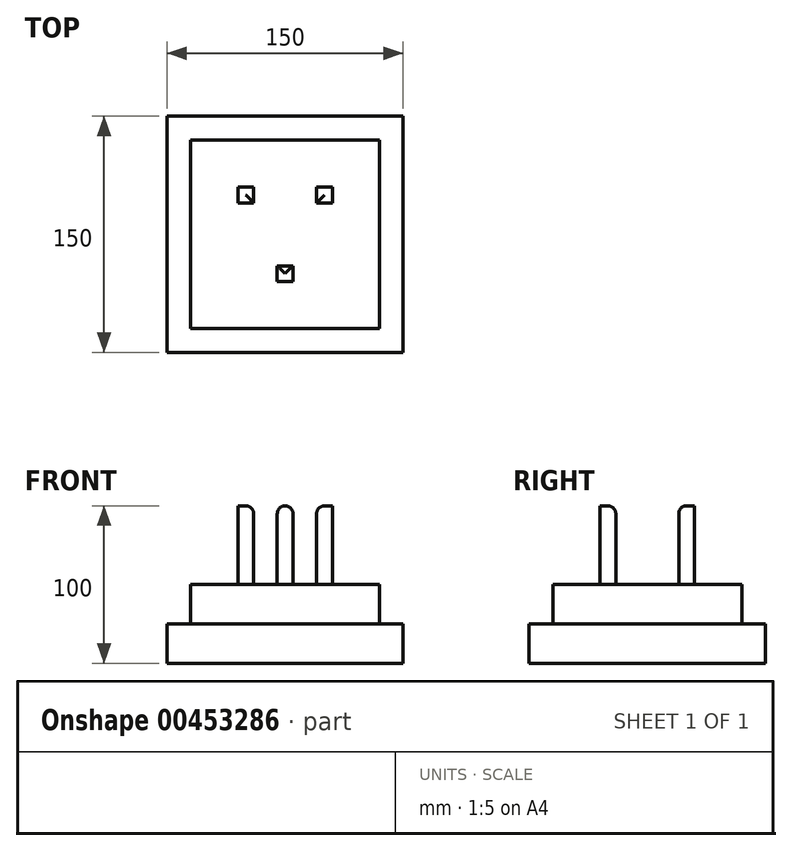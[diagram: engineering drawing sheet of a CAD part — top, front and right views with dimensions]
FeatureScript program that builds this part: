
annotation { "Feature Type Name" : "Feature", "Feature Type Description" : "" }
export const myFeature = defineFeature(function(context is Context, id is Id, definition is map)
    precondition{}
    {
        {
            var Q0;
            Q0=qCreatedBy(makeId("Top.planeOp"),FACE);
            var sketch = newSketch(context, id + "F0", { "sketchPlane" : qUnion([Q0])});
            skLineSegment(sketch, "E0.bottom", {"start": v(-75, 75) * mm, "end": v(75, 75) * mm});
            skLineSegment(sketch, "E0.top", {"start": v(-75, -75) * mm, "end": v(75, -75) * mm});
            skLineSegment(sketch, "E0.left", {"start": v(-75, 75) * mm, "end": v(-75, -75) * mm});
            skLineSegment(sketch, "E0.right", {"start": v(75, 75) * mm, "end": v(75, -75) * mm});
            skPoint(sketch, "E0.middle", {"position": v(0, 0) * mm});
            skSolve(sketch);
        }
        {
            var Q0;
            Q0=qSketchRegion(id+"F0",true);
            extrude(context, id + "F1", {"entities" : qUnion([Q0]), "depth" : 25 * mm});
        }
        {
            var Q0;
            Q0=makeQuery(id+"F1.opExtrude","CAP_FACE",FACE,{"disambiguationData":[OSD([sQuery(id+"F0.wireOp",EDGE,"E0.bottom"),sQuery(id+"F0.wireOp",EDGE,"E0.top"),sQuery(id+"F0.wireOp",EDGE,"E0.left"),sQuery(id+"F0.wireOp",EDGE,"E0.right")])],"isStart":false});
            var sketch = newSketch(context, id + "F2", { "sketchPlane" : qUnion([Q0])});
            skLineSegment(sketch, "E1.bottom", {"start": v(-60, 60) * mm, "end": v(60, 60) * mm});
            skLineSegment(sketch, "E1.top", {"start": v(-60, -60) * mm, "end": v(60, -60) * mm});
            skLineSegment(sketch, "E1.left", {"start": v(-60, 60) * mm, "end": v(-60, -60) * mm});
            skLineSegment(sketch, "E1.right", {"start": v(60, 60) * mm, "end": v(60, -60) * mm});
            skPoint(sketch, "E1.middle", {"position": v(0, 0) * mm});
            skSolve(sketch);
        }
        {
            var Q0;
            Q0=qSketchRegion(id+"F2",true);
            extrude(context, id + "F3", {"entities" : qUnion([Q0]), "operationType" : NewBodyOperationType.ADD, "depth" : 25 * mm});
        }
        {
            var Q0;
            Q0=makeQuery(id+"F3.opExtrude","CAP_FACE",FACE,{"disambiguationData":[OSD([sQuery(id+"F2.wireOp",EDGE,"E1.bottom"),sQuery(id+"F2.wireOp",EDGE,"E1.top"),sQuery(id+"F2.wireOp",EDGE,"E1.left"),sQuery(id+"F2.wireOp",EDGE,"E1.right")])],"isStart":false});
            var sketch = newSketch(context, id + "F4", { "sketchPlane" : qUnion([Q0])});
            skLineSegment(sketch, "E2.bottom", {"start": v(-5, -20) * mm, "end": v(5, -20) * mm});
            skLineSegment(sketch, "E2.top", {"start": v(-5, -30) * mm, "end": v(5, -30) * mm});
            skLineSegment(sketch, "E2.left", {"start": v(-5, -20) * mm, "end": v(-5, -30) * mm});
            skLineSegment(sketch, "E2.right", {"start": v(5, -20) * mm, "end": v(5, -30) * mm});
            skPoint(sketch, "E2.middle", {"position": v(0, -25) * mm});
            skLineSegment(sketch, "E3.bottom", {"start": v(-30, 30) * mm, "end": v(-20, 30) * mm});
            skLineSegment(sketch, "E3.top", {"start": v(-30, 20) * mm, "end": v(-20, 20) * mm});
            skLineSegment(sketch, "E3.left", {"start": v(-30, 30) * mm, "end": v(-30, 20) * mm});
            skLineSegment(sketch, "E3.right", {"start": v(-20, 30) * mm, "end": v(-20, 20) * mm});
            skPoint(sketch, "E3.middle", {"position": v(-25, 25) * mm});
            skLineSegment(sketch, "E4.bottom", {"start": v(30, 30) * mm, "end": v(20, 30) * mm});
            skLineSegment(sketch, "E4.top", {"start": v(30, 20) * mm, "end": v(20, 20) * mm});
            skLineSegment(sketch, "E4.left", {"start": v(30, 30) * mm, "end": v(30, 20) * mm});
            skLineSegment(sketch, "E4.right", {"start": v(20, 30) * mm, "end": v(20, 20) * mm});
            skPoint(sketch, "E4.middle", {"position": v(25, 25) * mm});
            skSolve(sketch);
        }
        {
            var Q0;
            Q0=qSketchRegion(id+"F4",true);
            extrude(context, id + "F5", {"entities" : qUnion([Q0]), "operationType" : NewBodyOperationType.ADD, "depth" : 50 * mm});
        }
        {
            var Q0;
            Q0=makeQuery(id+"F5.opExtrude","CAP_EDGE",EDGE,{"disambiguationData":[OSD([sQuery(id+"F4.wireOp",EDGE,"E3.top")])],"isStart":false});
            var Q1;
            Q1=makeQuery(id+"F5.opExtrude","CAP_EDGE",EDGE,{"disambiguationData":[OSD([sQuery(id+"F4.wireOp",EDGE,"E3.right")])],"isStart":false});
            var Q2;
            Q2=makeQuery(id+"F5.opExtrude","CAP_EDGE",EDGE,{"disambiguationData":[OSD([sQuery(id+"F4.wireOp",EDGE,"E4.top")])],"isStart":false});
            var Q3;
            Q3=makeQuery(id+"F5.opExtrude","CAP_EDGE",EDGE,{"disambiguationData":[OSD([sQuery(id+"F4.wireOp",EDGE,"E4.right")])],"isStart":false});
            var Q4;
            Q4=makeQuery(id+"F5.opExtrude","CAP_EDGE",EDGE,{"disambiguationData":[OSD([sQuery(id+"F4.wireOp",EDGE,"E2.left")])],"isStart":false});
            var Q5;
            Q5=makeQuery(id+"F5.opExtrude","CAP_EDGE",EDGE,{"disambiguationData":[OSD([sQuery(id+"F4.wireOp",EDGE,"E2.bottom")])],"isStart":false});
            var Q6;
            Q6=makeQuery(id+"F5.opExtrude","CAP_EDGE",EDGE,{"disambiguationData":[OSD([sQuery(id+"F4.wireOp",EDGE,"E2.right")])],"isStart":false});
            fillet(context, id + "F6", {"entities" : qUnion([Q0, Q1, Q2, Q3, Q4, Q5, Q6]), "radius" : 5 * mm, "tangentPropagation" : true, "allowEdgeOverflow" : false});
        }
    });
